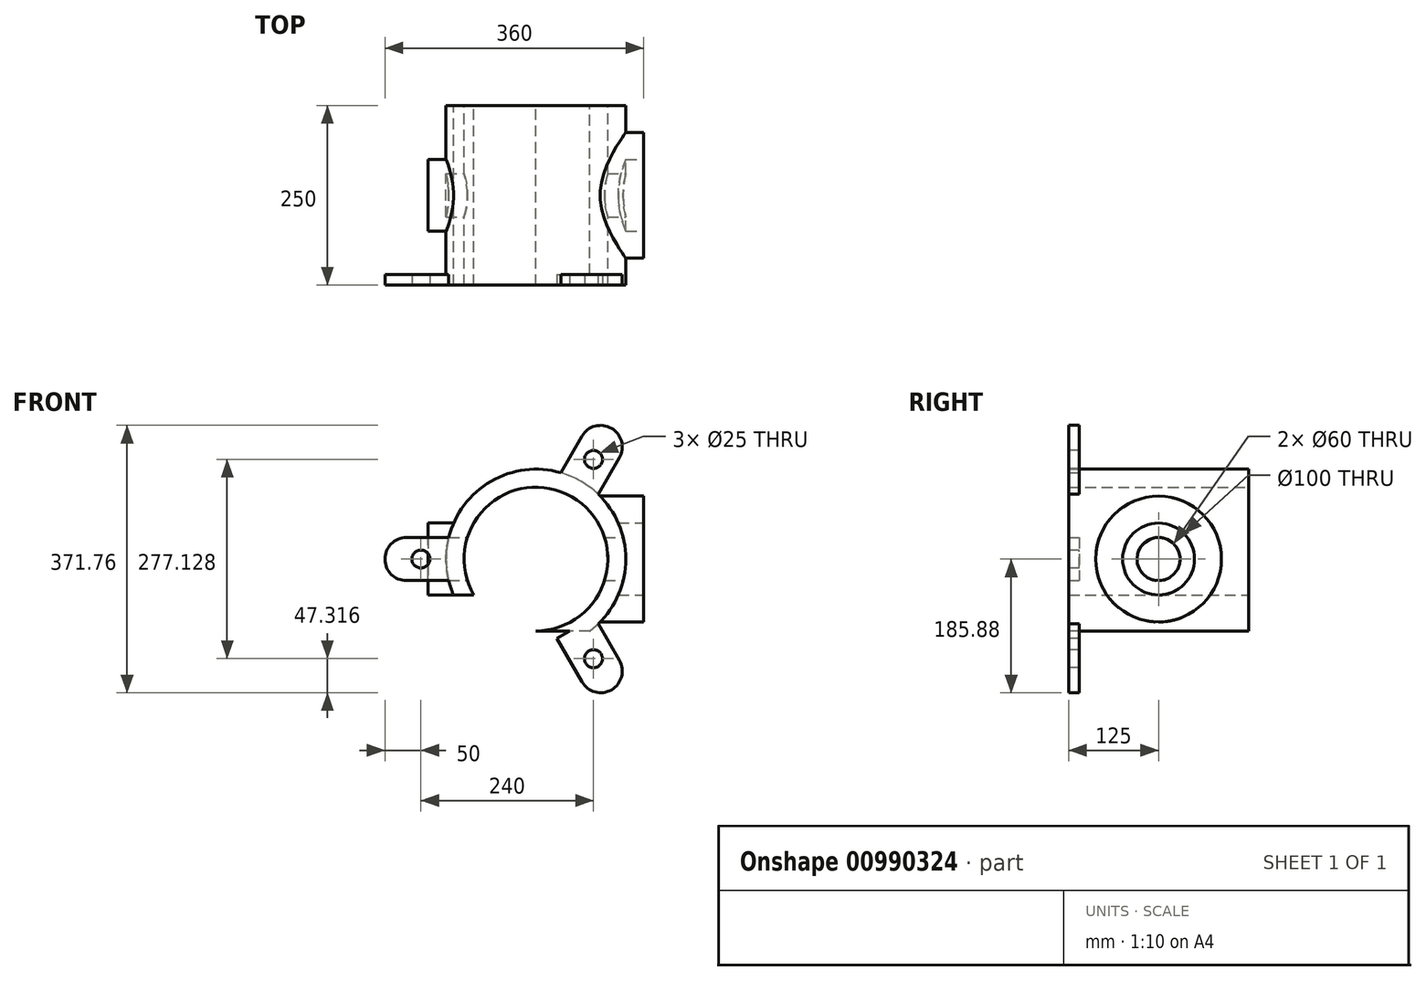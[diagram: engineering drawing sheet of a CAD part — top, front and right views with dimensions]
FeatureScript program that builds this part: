
annotation { "Feature Type Name" : "Feature", "Feature Type Description" : "" }
export const myFeature = defineFeature(function(context is Context, id is Id, definition is map)
    precondition{}
    {
        {
            var Q0;
            Q0=qCreatedBy(makeId("Front.planeOp"),FACE);
            var sketch = newSketch(context, id + "F0", { "sketchPlane" : qUnion([Q0])});
            skCircle(sketch, "E0", {"center": v(0, 0) * mm, "radius": 100 * mm});
            skCircle(sketch, "E1", {"center": v(0, 0) * mm, "radius": 125 * mm});
            skCircle(sketch, "E2", {"center": v(0, 0) * mm, "radius": 160 * mm});
            skLineSegment(sketch, "E3.bottom", {"start": v(150, 100) * mm, "end": v(-150, 100) * mm});
            skLineSegment(sketch, "E3.top", {"start": v(150, -100) * mm, "end": v(-150, -100) * mm});
            skLineSegment(sketch, "E3.left", {"start": v(150, 100) * mm, "end": v(150, -100) * mm});
            skLineSegment(sketch, "E3.right", {"start": v(-150, 100) * mm, "end": v(-150, -100) * mm});
            skLineSegment(sketch, "E4.bottom", {"start": v(240.07, 50) * mm, "end": v(-240.07, 50) * mm});
            skLineSegment(sketch, "E4.top", {"start": v(240.07, -50) * mm, "end": v(-240.07, -50) * mm});
            skLineSegment(sketch, "E4.left", {"start": v(240.07, 50) * mm, "end": v(240.07, -50) * mm});
            skLineSegment(sketch, "E4.right", {"start": v(-240.07, 50) * mm, "end": v(-240.07, -50) * mm});
            skSolve(sketch);
        }
        {
            var Q0;
            {var subQ0=sQuery(id+"F0.wireOp",EDGE,"E3.bottom");var subQ1=sQuery(id+"F0.wireOp",EDGE,"E0");var subQ2=makeQuery(id+"F0.imprint","INTERSECT",VERTEX,{"derivedFrom":[subQ1,subQ0]});Q0=makeQuery(id+"F0.imprint","IMPRINT",FACE,{"disambiguationData":[TD([[makeQuery(id+"F0.imprint","IMPRINT",EDGE,{"disambiguationData":[TD([[subQ2,-1.0]])],"derivedFrom":subQ1}),-1.0]])]});}
            var Q1;
            {var subQ0=sQuery(id+"F0.wireOp",EDGE,"E3.bottom");var subQ1=sQuery(id+"F0.wireOp",EDGE,"E1");var subQ2=makeQuery(id+"F0.imprint","INTERSECT",VERTEX,{"disambiguationData":[OD(0.0)],"derivedFrom":[subQ1,subQ0]});Q1=makeQuery(id+"F0.imprint","IMPRINT",FACE,{"disambiguationData":[TD([[makeQuery(id+"F0.imprint","IMPRINT",EDGE,{"disambiguationData":[TD([[subQ2,1.0]])],"derivedFrom":subQ1}),1.0]])]});}
            var Q2;
            {var subQ0=sQuery(id+"F0.wireOp",EDGE,"E3.bottom");var subQ1=sQuery(id+"F0.wireOp",EDGE,"E0");var subQ2=makeQuery(id+"F0.imprint","INTERSECT",VERTEX,{"derivedFrom":[subQ1,subQ0]});Q2=makeQuery(id+"F0.imprint","IMPRINT",FACE,{"disambiguationData":[TD([[makeQuery(id+"F0.imprint","IMPRINT",EDGE,{"disambiguationData":[TD([[subQ2,1.0]])],"derivedFrom":subQ1}),-1.0]])]});}
            var Q3;
            {var subQ0=sQuery(id+"F0.wireOp",EDGE,"E3.top");var subQ1=sQuery(id+"F0.wireOp",EDGE,"E1");var subQ2=makeQuery(id+"F0.imprint","INTERSECT",VERTEX,{"disambiguationData":[OD(0.0)],"derivedFrom":[subQ1,subQ0]});Q3=makeQuery(id+"F0.imprint","IMPRINT",FACE,{"disambiguationData":[TD([[makeQuery(id+"F0.imprint","IMPRINT",EDGE,{"disambiguationData":[TD([[subQ2,-1.0]])],"derivedFrom":subQ1}),1.0]])]});}
            var Q4;
            {var subQ0=sQuery(id+"F0.wireOp",EDGE,"E4.bottom");var subQ1=sQuery(id+"F0.wireOp",EDGE,"E0");var subQ2=makeQuery(id+"F0.imprint","INTERSECT",VERTEX,{"disambiguationData":[OD(1.0)],"derivedFrom":[subQ1,subQ0]});Q4=makeQuery(id+"F0.imprint","IMPRINT",FACE,{"disambiguationData":[TD([[makeQuery(id+"F0.imprint","IMPRINT",EDGE,{"disambiguationData":[TD([[subQ2,-1.0]])],"derivedFrom":subQ1}),-1.0]])]});}
            var Q5;
            {var subQ0=sQuery(id+"F0.wireOp",EDGE,"E4.top");var subQ1=sQuery(id+"F0.wireOp",EDGE,"E0");var subQ2=makeQuery(id+"F0.imprint","INTERSECT",VERTEX,{"disambiguationData":[OD(0.0)],"derivedFrom":[subQ1,subQ0]});Q5=makeQuery(id+"F0.imprint","IMPRINT",FACE,{"disambiguationData":[TD([[makeQuery(id+"F0.imprint","IMPRINT",EDGE,{"disambiguationData":[TD([[subQ2,-1.0]])],"derivedFrom":subQ1}),-1.0]])]});}
            var Q6;
            {var subQ0=sQuery(id+"F0.wireOp",EDGE,"E3.top");var subQ1=sQuery(id+"F0.wireOp",EDGE,"E0");var subQ2=makeQuery(id+"F0.imprint","INTERSECT",VERTEX,{"derivedFrom":[subQ1,subQ0]});Q6=makeQuery(id+"F0.imprint","IMPRINT",FACE,{"disambiguationData":[TD([[makeQuery(id+"F0.imprint","IMPRINT",EDGE,{"disambiguationData":[TD([[subQ2,-1.0]])],"derivedFrom":subQ1}),-1.0]])]});}
            var Q7;
            {var subQ0=sQuery(id+"F0.wireOp",EDGE,"E4.bottom");var subQ1=sQuery(id+"F0.wireOp",EDGE,"E0");var subQ2=makeQuery(id+"F0.imprint","INTERSECT",VERTEX,{"disambiguationData":[OD(0.0)],"derivedFrom":[subQ1,subQ0]});Q7=makeQuery(id+"F0.imprint","IMPRINT",FACE,{"disambiguationData":[TD([[makeQuery(id+"F0.imprint","IMPRINT",EDGE,{"disambiguationData":[TD([[subQ2,1.0]])],"derivedFrom":subQ1}),-1.0]])]});}
            var Q8;
            {var subQ0=sQuery(id+"F0.wireOp",EDGE,"E3.bottom");var subQ1=sQuery(id+"F0.wireOp",EDGE,"E1");var subQ2=makeQuery(id+"F0.imprint","INTERSECT",VERTEX,{"disambiguationData":[OD(0.0)],"derivedFrom":[subQ1,subQ0]});Q8=makeQuery(id+"F0.imprint","IMPRINT",FACE,{"disambiguationData":[TD([[makeQuery(id+"F0.imprint","IMPRINT",EDGE,{"disambiguationData":[TD([[subQ2,-1.0]])],"derivedFrom":subQ1}),1.0]])]});}
            extrude(context, id + "F1", {"entities" : qUnion([Q0, Q1, Q2, Q3, Q4, Q5, Q6, Q7, Q8]), "endBound" : BoundingType.SYMMETRIC, "depth" : 250 * mm, "offsetDistance" : 25 * mm});
        }
        {
            var Q0;
            Q0=qCreatedBy(makeId("Right.planeOp"),FACE);
            cPlane(context, id + "F2", {"entities" : qUnion([Q0]), "cplaneType" : CPlaneType.OFFSET, "offset" : 150 * mm, "width" : 150 * mm, "height" : 150 * mm});
        }
        {
            var Q0;
            Q0=qCreatedBy(id+"F2.planeOp",FACE);
            var sketch = newSketch(context, id + "F3", { "sketchPlane" : qUnion([Q0])});
            skCircle(sketch, "E5", {"center": v(0, 0) * mm, "radius": 87.5 * mm});
            skCircle(sketch, "E6", {"center": v(0, 0) * mm, "radius": 50 * mm});
            skCircle(sketch, "E7", {"center": v(0, 0) * mm, "radius": 30 * mm});
            skSolve(sketch);
        }
        {
            var Q0;
            Q0 = qSketchRegion(id + "F3", true);
            var Q1;
            Q1=makeQuery(id+"F1.opExtrude","SWEPT_FACE",FACE,{"disambiguationData":[OSD([sQuery(id+"F0.wireOp",EDGE,"E1")])]});
            extrude(context, id + "F4", {"entities" : qUnion([Q0]), "operationType" : NewBodyOperationType.ADD, "endBound" : BoundingType.UP_TO_SURFACE, "oppositeDirection" : true, "depth" : 84 * mm, "endBoundEntityFace" : qUnion([Q1]), "offsetDistance" : 25 * mm});
        }
        {
            var Q0;
            Q0=makeQuery(id+"F3.imprint","IMPRINT",FACE,{"disambiguationData":[TD([[makeQuery(id+"F3.imprint","IMPRINT",EDGE,{"derivedFrom":sQuery(id+"F3.wireOp",EDGE,"E7")}),1.0]])]});
            extrude(context, id + "F5", {"entities" : qUnion([Q0]), "operationType" : NewBodyOperationType.REMOVE, "oppositeDirection" : true, "depth" : 275 * mm, "offsetDistance" : 25 * mm});
        }
        {
            var Q0;
            Q0=qCreatedBy(makeId("Right.planeOp"),FACE);
            cPlane(context, id + "F6", {"entities" : qUnion([Q0]), "cplaneType" : CPlaneType.OFFSET, "offset" : 150 * mm, "oppositeDirection" : true, "width" : 150 * mm, "height" : 150 * mm});
        }
        {
            var Q0;
            Q0=qCreatedBy(id+"F6.planeOp",FACE);
            var sketch = newSketch(context, id + "F7", { "sketchPlane" : qUnion([Q0])});
            skCircle(sketch, "E8", {"center": v(0, 0) * mm, "radius": 50 * mm});
            skSolve(sketch);
        }
        {
            var Q0;
            Q0 = qSketchRegion(id + "F7", true);
            var Q1;
            {var subQ0=sQuery(id+"F0.wireOp",EDGE,"E1");Q1=makeQuery(id+"F4.boolean.opBoolean","SPLIT",FACE,{"disambiguationData":[TD([makeQuery(id+"F4.opExtrude","SWEPT_FACE",FACE,{"disambiguationData":[OSD([sQuery(id+"F3.wireOp",EDGE,"E5")])]})])],"derivedFrom":makeQuery(id+"F1.opExtrude","SWEPT_FACE",FACE,{"disambiguationData":[OSD([subQ0])]})});}
            extrude(context, id + "F8", {"entities" : qUnion([Q0]), "operationType" : NewBodyOperationType.ADD, "endBound" : BoundingType.UP_TO_SURFACE, "depth" : 25 * mm, "endBoundEntityFace" : qUnion([Q1]), "offsetDistance" : 25 * mm});
        }
        {
            var Q0;
            Q0=qCreatedBy(makeId("Front.planeOp"),FACE);
            cPlane(context, id + "F9", {"entities" : qUnion([Q0]), "cplaneType" : CPlaneType.OFFSET, "offset" : 125 * mm, "width" : 150 * mm, "height" : 150 * mm});
        }
        {
            var Q0;
            Q0=qCreatedBy(id+"F9.planeOp",FACE);
            var sketch = newSketch(context, id + "F10", { "sketchPlane" : qUnion([Q0])});
            skCircle(sketch, "E9", {"center": v(0, 0) * mm, "radius": 160 * mm});
            skLineSegment(sketch, "E10.bottom", {"start": v(-110, 30) * mm, "end": v(-210, 30) * mm});
            skLineSegment(sketch, "E10.top", {"start": v(-110, -30) * mm, "end": v(-210, -30) * mm});
            skLineSegment(sketch, "E10.left", {"start": v(-110, 30) * mm, "end": v(-110, -30) * mm});
            skLineSegment(sketch, "E10.right", {"start": v(-210, 30) * mm, "end": v(-210, -30) * mm});
            skPoint(sketch, "E10.middle", {"position": v(-160, 0) * mm});
            skCircle(sketch, "E11", {"center": v(-160, 0) * mm, "radius": 12.5 * mm});
            skSolve(sketch);
        }
        {
            var Q0;
            {var subQ5=sQuery(id+"F10.wireOp",EDGE,"E10.right");Q0=makeQuery(id+"F10.imprint","IMPRINT",FACE,{"disambiguationData":[TD([[makeQuery(id+"F10.imprint","IMPRINT",EDGE,{"derivedFrom":subQ5}),1.0]])]});}
            var Q1;
            {var subQ5=sQuery(id+"F10.wireOp",EDGE,"E10.left");Q1=makeQuery(id+"F10.imprint","IMPRINT",FACE,{"disambiguationData":[TD([[makeQuery(id+"F10.imprint","IMPRINT",EDGE,{"derivedFrom":subQ5}),-1.0]])]});}
            extrude(context, id + "F11", {"entities" : qUnion([Q0, Q1]), "oppositeDirection" : true, "depth" : 15 * mm, "offsetDistance" : 25 * mm});
        }
        {
            var Q0;
            Q0=makeQuery(id+"F11.opExtrude","SWEPT_EDGE",EDGE,{"disambiguationData":[OSD([sQuery(id+"F10.wireOp",EDGE,"E10.top"),sQuery(id+"F10.wireOp",EDGE,"E10.right")])]});
            var Q1;
            Q1=makeQuery(id+"F11.opExtrude","SWEPT_EDGE",EDGE,{"disambiguationData":[OSD([sQuery(id+"F10.wireOp",EDGE,"E10.bottom"),sQuery(id+"F10.wireOp",EDGE,"E10.right")])]});
            fillet(context, id + "F12", {"entities" : qUnion([Q0, Q1]), "radius" : 30 * mm, "tangentPropagation" : true, "allowEdgeOverflow" : false});
        }
        {
            var Q0;
            Q0=makeQuery(id+"F11.opExtrude","SWEPT_BODY",BODY,{"disambiguationData":[OSD([sQuery(id+"F10.wireOp",EDGE,"E10.bottom"),sQuery(id+"F10.wireOp",EDGE,"E10.top"),sQuery(id+"F10.wireOp",EDGE,"E10.left"),sQuery(id+"F10.wireOp",EDGE,"E10.right"),sQuery(id+"F10.wireOp",EDGE,"E11")])]});
            var Q1;
            Q1=makeQuery(id+"F1.opExtrude","CAP_EDGE",EDGE,{"disambiguationData":[OSD([sQuery(id+"F0.wireOp",EDGE,"E1")])],"isStart":false});
            circularPattern(context, id + "F13", {"operationType" : NewBodyOperationType.ADD, "entities" : qUnion([Q0]), "axis" : qUnion([Q1]), "angle" : 360 * degree, "instanceCount" : 3, "equalSpace" : true});
        }
    });
